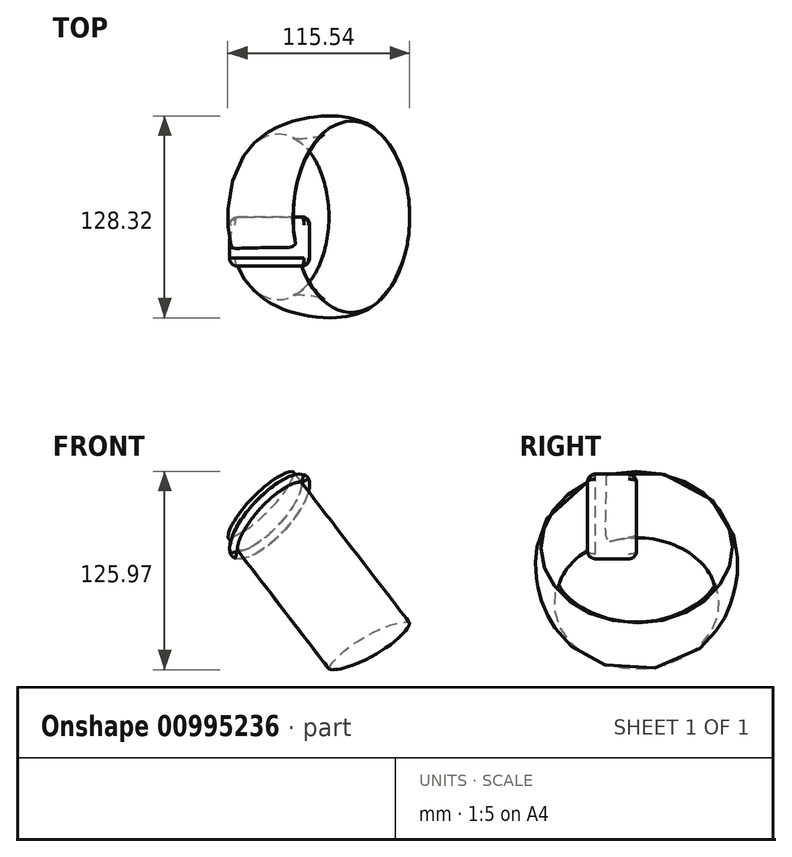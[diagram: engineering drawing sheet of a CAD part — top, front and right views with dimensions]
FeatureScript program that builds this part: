
annotation { "Feature Type Name" : "Feature", "Feature Type Description" : "" }
export const myFeature = defineFeature(function(context is Context, id is Id, definition is map)
    precondition{}
    {
        {
            var Q0;
            Q0=qCreatedBy(makeId("Front.planeOp"),FACE);
            var sketch = newSketch(context, id + "F0", { "sketchPlane" : qUnion([Q0])});
            skEllipse(sketch, "E0", {"center": v(-23.2, 50.86) * mm, "majorRadius": 34.74 * mm, "minorRadius": 12.89 * mm, "majorAxis": v(-0.68, -0.73)});
            skSolve(sketch);
        }
        {
            var Q0;
            Q0=makeQuery(id+"F0.imprint","IMPRINT",FACE,{"disambiguationData":[TD([[makeQuery(id+"F0.imprint","IMPRINT",EDGE,{"derivedFrom":sQuery(id+"F0.wireOp",EDGE,"E0")}),1.0]])]});
            var Q1;
            Q1 = qSketchRegion(id + "F3BUmFBfgHCsw3P_0", true);
            extrude(context, id + "F1", {"entities" : qUnion([Q0, Q1]), "depth" : 31.28 * mm, "offsetDistance" : 25.4 * mm});
        }
        {
            var Q0;
            Q0=makeQuery(id+"F1.opExtrude","CAP_EDGE",EDGE,{"disambiguationData":[OSD([sQuery(id+"F0.wireOp",EDGE,"E0")])],"isStart":false});
            var Q1;
            Q1=makeQuery(id+"F1.opExtrude","CAP_EDGE",EDGE,{"disambiguationData":[OSD([sQuery(id+"F0.wireOp",EDGE,"E0")])],"isStart":true});
            fillet(context, id + "F2", {"entities" : qUnion([Q0, Q1]), "radius" : 5.08 * mm, "tangentPropagation" : true, "allowEdgeOverflow" : false});
        }
        {
            var Q0;
            Q0=qCreatedBy(makeId("Front.planeOp"),FACE);
            var sketch = newSketch(context, id + "F3", { "sketchPlane" : qUnion([Q0])});
            skLineSegment(sketch, "E1", {"start": v(48.16, 46.29) * mm, "end": v(-69.6, -44.34) * mm});
            skSolve(sketch);
        }
        {
            var Q0;
            Q0=makeQuery(id+"F1.opExtrude","CAP_FACE",FACE,{"disambiguationData":[OSD([sQuery(id+"F0.wireOp",EDGE,"E0")])],"isStart":false});
            var Q1;
            Q1 = qSketchRegion(id + "F3BUmFBfgHCsw3P_0", true);
            var Q2;
            Q2=sQuery(id+"F3.wireOp",EDGE,"E1");
            revolve(context, id + "F4", {"operationType" : NewBodyOperationType.ADD, "surfaceOperationType" : NewSurfaceOperationType.NEW, "entities" : qUnion([Q0, Q1]), "axis" : qUnion([Q2]), "revolveType" : RevolveType.FULL});
        }
    });
